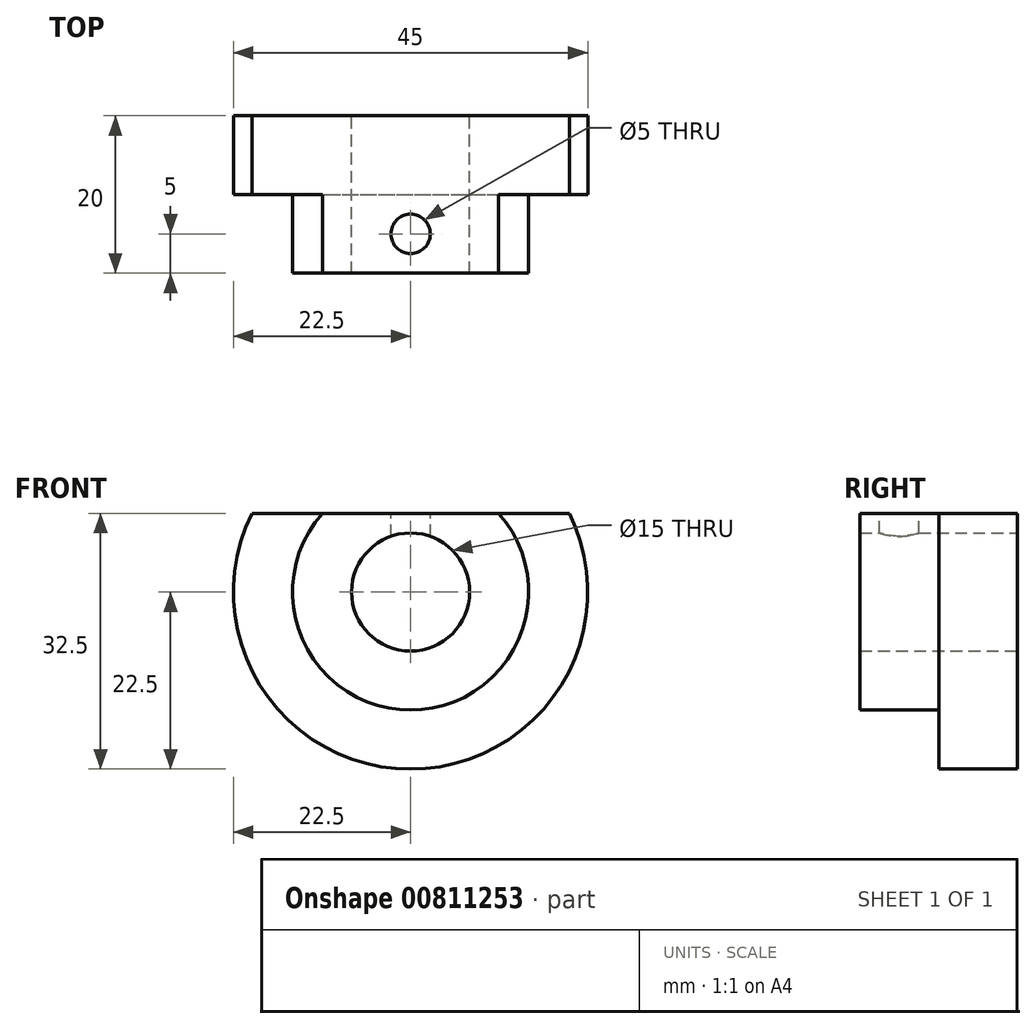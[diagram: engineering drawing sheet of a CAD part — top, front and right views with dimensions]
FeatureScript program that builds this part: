
annotation { "Feature Type Name" : "Feature", "Feature Type Description" : "" }
export const myFeature = defineFeature(function(context is Context, id is Id, definition is map)
    precondition{}
    {
        {
            var Q0;
            Q0=qCreatedBy(makeId("Front.planeOp"),FACE);
            var sketch = newSketch(context, id + "F0", { "sketchPlane" : qUnion([Q0])});
            skArc(sketch, "E0", {"start": v(-11.18, 10) * mm, "mid": v(0, -15) * mm, "end": v(11.18, 10) * mm});
            skArc(sketch, "E1", {"start": v(-20.16, 10) * mm, "mid": v(0, -22.5) * mm, "end": v(20.16, 10) * mm});
            skLineSegment(sketch, "E2", {"start": v(-20.16, 10) * mm, "end": v(20.16, 10) * mm});
            skCircle(sketch, "E3", {"center": v(0, 0) * mm, "radius": 7.5 * mm});
            skSolve(sketch);
        }
        {
            var Q0;
            Q0 = qSketchRegion(id + "F0", true);
            extrude(context, id + "F1", {"entities" : qUnion([Q0]), "depth" : 10 * mm, "offsetDistance" : 25 * mm});
        }
        {
            var Q0;
            {var subQ0=sQuery(id+"F0.wireOp",EDGE,"E0");Q0=makeQuery(id+"F0.imprint","IMPRINT",FACE,{"disambiguationData":[TD([[makeQuery(id+"F0.imprint","IMPRINT",EDGE,{"derivedFrom":subQ0}),1.0]])]});}
            extrude(context, id + "F2", {"entities" : qUnion([Q0]), "operationType" : NewBodyOperationType.ADD, "depth" : 20 * mm, "offsetDistance" : 25 * mm});
        }
        {
            var Q0;
            {var subQ0=sQuery(id+"F0.wireOp",EDGE,"E2");Q0=makeQuery(id+"F2.boolean.opBoolean","MERGE",FACE,{"derivedFrom":[makeQuery(id+"F1.opExtrude","SWEPT_FACE",FACE,{"disambiguationData":[OSD([subQ0])]}),makeQuery(id+"F2.opExtrude","SWEPT_FACE",FACE,{"disambiguationData":[OSD([subQ0])]})]});}
            var sketch = newSketch(context, id + "F3", { "sketchPlane" : qUnion([Q0])});
            skCircle(sketch, "E4", {"center": v(0, -15) * mm, "radius": 2.5 * mm});
            skSolve(sketch);
        }
        {
            var Q0;
            Q0 = qSketchRegion(id + "F3", true);
            var Q1;
            {var subQ0=sQuery(id+"F0.wireOp",EDGE,"E3");Q1=makeQuery(id+"F2.boolean.opBoolean","MERGE",FACE,{"derivedFrom":[makeQuery(id+"F1.opExtrude","SWEPT_FACE",FACE,{"disambiguationData":[OSD([subQ0])]}),makeQuery(id+"F2.opExtrude","SWEPT_FACE",FACE,{"disambiguationData":[OSD([subQ0])]})]});}
            extrude(context, id + "F4", {"entities" : qUnion([Q0]), "operationType" : NewBodyOperationType.REMOVE, "endBound" : BoundingType.UP_TO_SURFACE, "oppositeDirection" : true, "depth" : 25 * mm, "endBoundEntityFace" : qUnion([Q1]), "offsetDistance" : 25 * mm});
        }
    });
